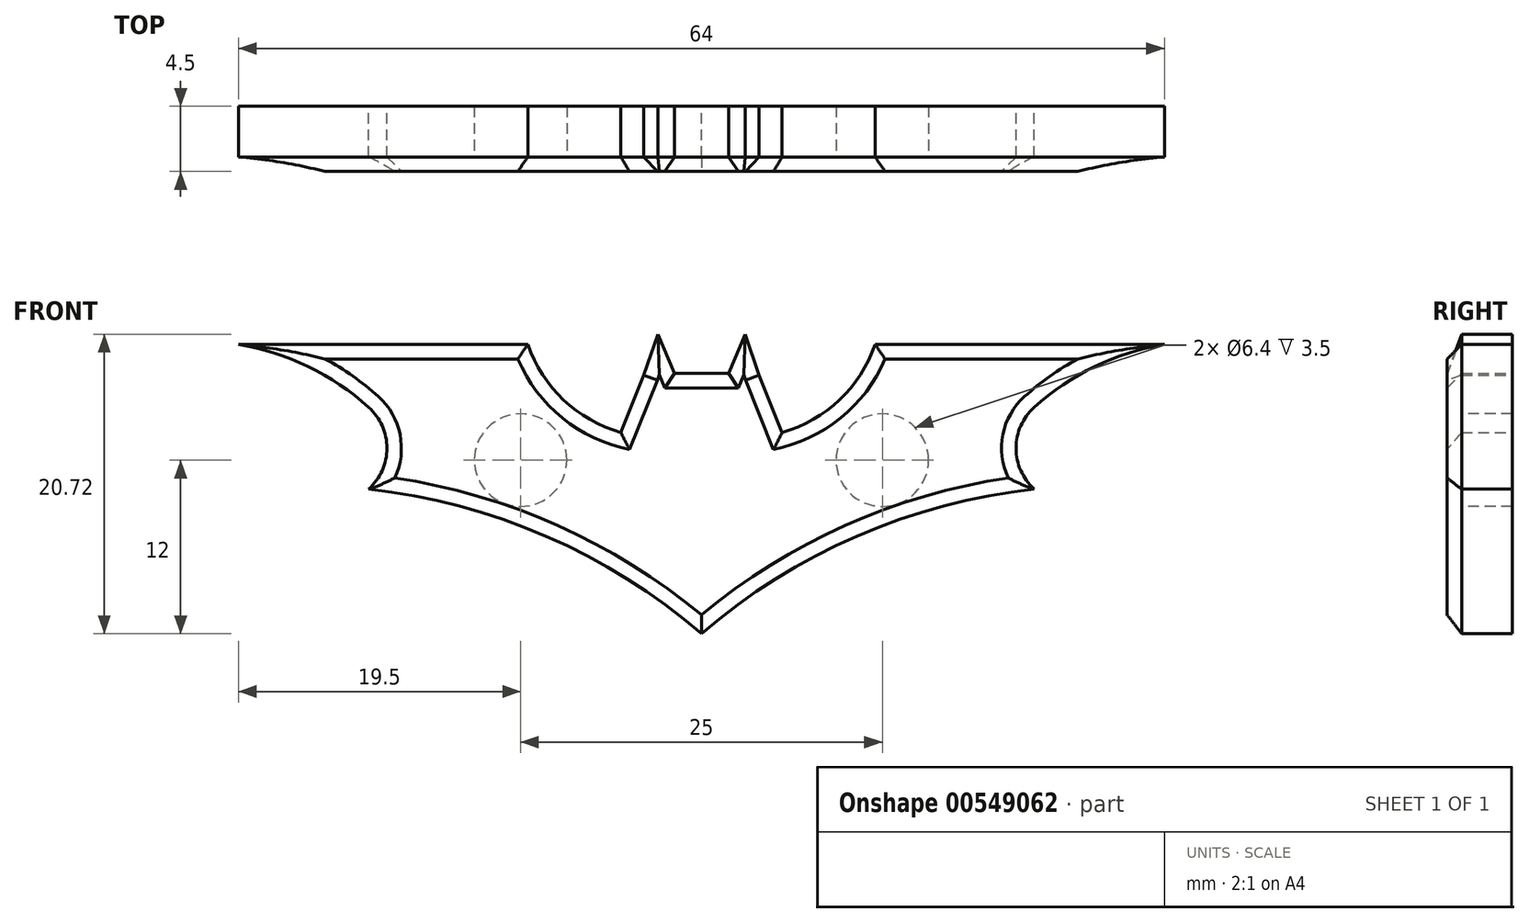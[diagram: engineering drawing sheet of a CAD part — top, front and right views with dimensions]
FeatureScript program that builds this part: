
annotation { "Feature Type Name" : "Feature", "Feature Type Description" : "" }
export const myFeature = defineFeature(function(context is Context, id is Id, definition is map)
    precondition{}
    {
        {
            var Q0;
            Q0=qCreatedBy(makeId("Front.planeOp"),FACE);
            var sketch = newSketch(context, id + "F0", { "sketchPlane" : qUnion([Q0])});
            skLineSegment(sketch, "E0", {"start": v(0, 0) * mm, "end": v(-12.5, 0) * mm, "construction": true});
            skLineSegment(sketch, "E1", {"start": v(0, 0) * mm, "end": v(12.5, 0) * mm, "construction": true});
            skCircle(sketch, "E2", {"center": v(-12.5, 0) * mm, "radius": 3.2 * mm});
            skCircle(sketch, "E3", {"center": v(12.5, 0) * mm, "radius": 3.2 * mm});
            skLineSegment(sketch, "E4", {"start": v(0, 6) * mm, "end": v(-1.87, 6) * mm});
            skLineSegment(sketch, "E5", {"start": v(-1.87, 6) * mm, "end": v(-3, 8.72) * mm});
            skLineSegment(sketch, "E6", {"start": v(-3, 8.72) * mm, "end": v(-3.98, 5.86) * mm});
            skLineSegment(sketch, "E7", {"start": v(-3.98, 5.86) * mm, "end": v(-5.58, 1.92) * mm});
            skArc(sketch, "E8", {"start": v(-12, 8) * mm, "mid": v(-9.53, 4.17) * mm, "end": v(-5.58, 1.92) * mm});
            skLineSegment(sketch, "E9", {"start": v(-12, 8) * mm, "end": v(-32, 8) * mm});
            skArc(sketch, "E10", {"start": v(-23, 3.66) * mm, "mid": v(-27.19, 6.47) * mm, "end": v(-32, 8) * mm});
            skArc(sketch, "E11", {"start": v(-23, -2) * mm, "mid": v(-21.74, 0.83) * mm, "end": v(-23, 3.66) * mm});
            skArc(sketch, "E12", {"start": v(0, -12) * mm, "mid": v(-10.74, -5.26) * mm, "end": v(-23, -2) * mm});
            skLineSegment(sketch, "E13.MirrorCS", {"start": v(0, 6) * mm, "end": v(1.87, 6) * mm});
            skLineSegment(sketch, "E14.MirrorCS", {"start": v(1.87, 6) * mm, "end": v(3, 8.72) * mm});
            skLineSegment(sketch, "E15.MirrorCS", {"start": v(3, 8.72) * mm, "end": v(3.98, 5.86) * mm});
            skLineSegment(sketch, "E16.MirrorCS", {"start": v(3.98, 5.86) * mm, "end": v(5.58, 1.92) * mm});
            skArc(sketch, "E17.MirrorCS", {"start": v(12, 8) * mm, "mid": v(9.53, 4.17) * mm, "end": v(5.58, 1.92) * mm});
            skLineSegment(sketch, "E18.MirrorCS", {"start": v(12, 8) * mm, "end": v(32, 8) * mm});
            skArc(sketch, "E19.MirrorCS", {"start": v(23, 3.66) * mm, "mid": v(27.19, 6.47) * mm, "end": v(32, 8) * mm});
            skArc(sketch, "E20.MirrorCS", {"start": v(23, -2) * mm, "mid": v(21.74, 0.83) * mm, "end": v(23, 3.66) * mm});
            skArc(sketch, "E21.MirrorCS", {"start": v(0, -12) * mm, "mid": v(10.74, -5.26) * mm, "end": v(23, -2) * mm});
            skSolve(sketch);
        }
        {
            var Q0;
            Q0=makeQuery(id+"F0.imprint","IMPRINT",FACE,{"disambiguationData":[TD([[makeQuery(id+"F0.imprint","IMPRINT",EDGE,{"derivedFrom":sQuery(id+"F0.wireOp",EDGE,"E2")}),1.0]])]});
            var Q1;
            Q1=makeQuery(id+"F0.imprint","IMPRINT",FACE,{"disambiguationData":[TD([[makeQuery(id+"F0.imprint","IMPRINT",EDGE,{"derivedFrom":sQuery(id+"F0.wireOp",EDGE,"E2")}),-1.0]])]});
            var Q2;
            Q2=makeQuery(id+"F0.imprint","IMPRINT",FACE,{"disambiguationData":[TD([[makeQuery(id+"F0.imprint","IMPRINT",EDGE,{"derivedFrom":sQuery(id+"F0.wireOp",EDGE,"E3")}),1.0]])]});
            extrude(context, id + "F1", {"entities" : qUnion([Q0, Q1, Q2]), "depth" : 1 * mm, "offsetDistance" : 25 * mm});
        }
        {
            var Q0;
            Q0 = qSketchRegion(id + "F0", true);
            extrude(context, id + "F2", {"entities" : qUnion([Q0]), "operationType" : NewBodyOperationType.ADD, "oppositeDirection" : true, "depth" : 3.5 * mm, "offsetDistance" : 25 * mm});
        }
        {
            var Q0;
            Q0=makeQuery(id+"F1.opExtrude","CAP_FACE",FACE,{"disambiguationData":[OSD([sQuery(id+"F0.wireOp",EDGE,"E4"),sQuery(id+"F0.wireOp",EDGE,"E5"),sQuery(id+"F0.wireOp",EDGE,"E6"),sQuery(id+"F0.wireOp",EDGE,"E7"),sQuery(id+"F0.wireOp",EDGE,"E8"),sQuery(id+"F0.wireOp",EDGE,"E9"),sQuery(id+"F0.wireOp",EDGE,"E10"),sQuery(id+"F0.wireOp",EDGE,"E11"),sQuery(id+"F0.wireOp",EDGE,"E12"),sQuery(id+"F0.wireOp",EDGE,"E13.MirrorCS"),sQuery(id+"F0.wireOp",EDGE,"E14.MirrorCS"),sQuery(id+"F0.wireOp",EDGE,"E15.MirrorCS"),sQuery(id+"F0.wireOp",EDGE,"E16.MirrorCS"),sQuery(id+"F0.wireOp",EDGE,"E17.MirrorCS"),sQuery(id+"F0.wireOp",EDGE,"E18.MirrorCS"),sQuery(id+"F0.wireOp",EDGE,"E19.MirrorCS"),sQuery(id+"F0.wireOp",EDGE,"E20.MirrorCS"),sQuery(id+"F0.wireOp",EDGE,"E21.MirrorCS")])],"isStart":false});
            chamfer(context, id + "F3", {"entities" : qUnion([Q0]), "width" : 1 * mm, "tangentPropagation" : true});
        }
    });
